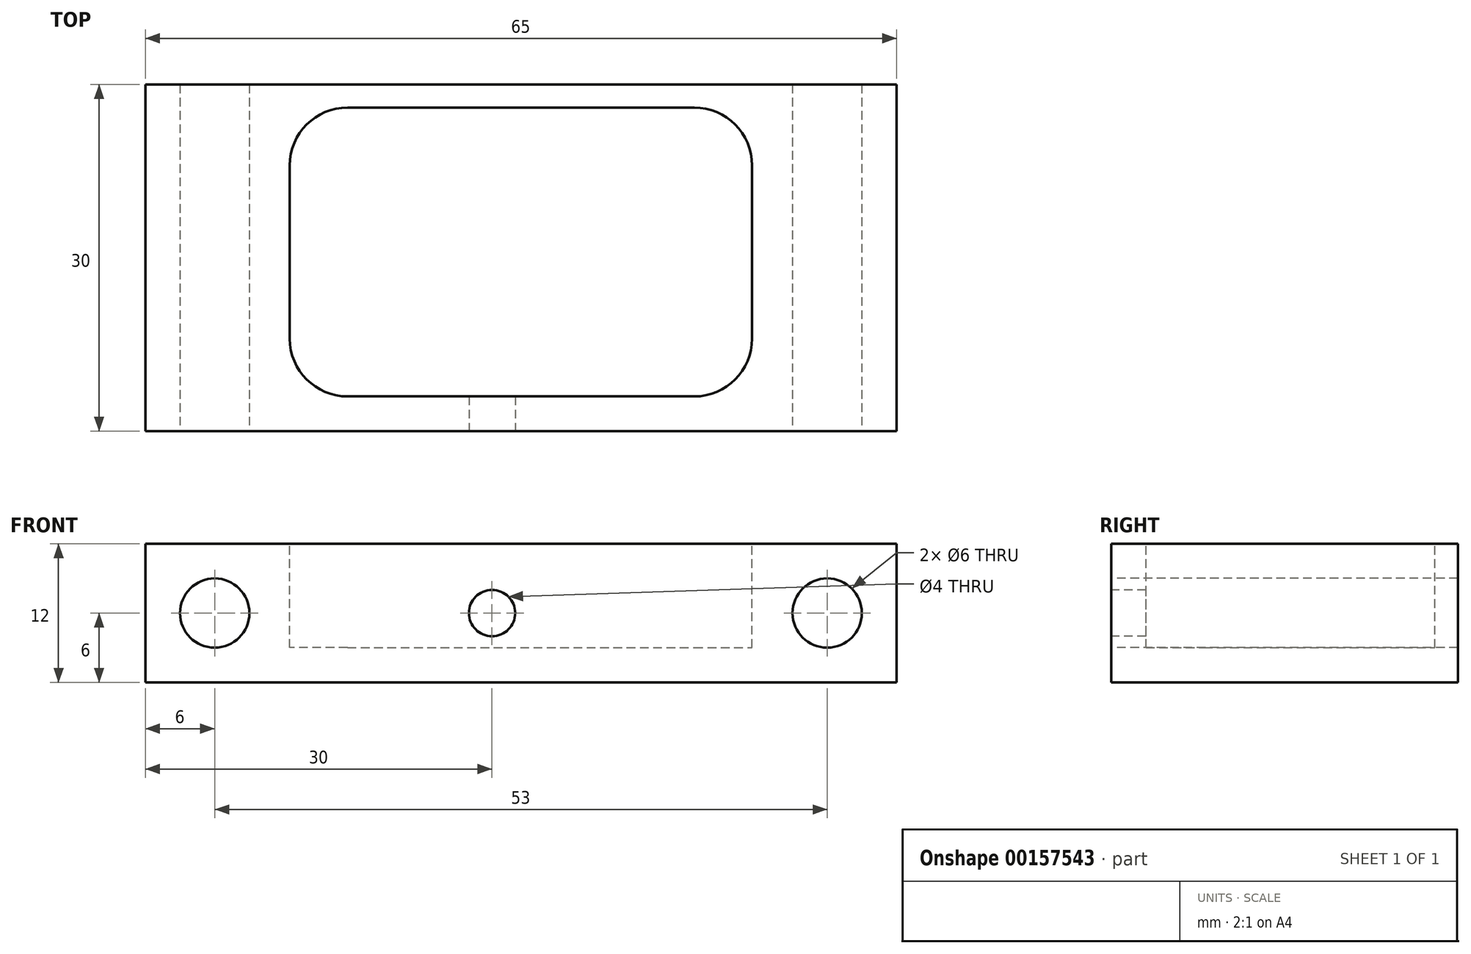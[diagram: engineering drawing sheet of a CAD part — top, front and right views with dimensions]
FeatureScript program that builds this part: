
annotation { "Feature Type Name" : "Feature", "Feature Type Description" : "" }
export const myFeature = defineFeature(function(context is Context, id is Id, definition is map)
    precondition{}
    {
        {
            var Q0;
            Q0=qCreatedBy(makeId("Top.planeOp"),FACE);
            var sketch = newSketch(context, id + "F0", { "sketchPlane" : qUnion([Q0])});
            skLineSegment(sketch, "E0.bottom", {"start": v(-22.35, 5.59) * mm, "end": v(42.65, 5.59) * mm});
            skLineSegment(sketch, "E0.top", {"start": v(-22.35, -24.41) * mm, "end": v(42.65, -24.41) * mm});
            skLineSegment(sketch, "E0.left", {"start": v(-22.35, 5.59) * mm, "end": v(-22.35, -24.41) * mm});
            skLineSegment(sketch, "E0.right", {"start": v(42.65, 5.59) * mm, "end": v(42.65, -24.41) * mm});
            skSolve(sketch);
        }
        {
            var Q0;
            {var subQ2=sQuery(id+"F0.wireOp",EDGE,"E0.bottom");Q0=makeQuery(id+"F0.imprint","IMPRINT",FACE,{"disambiguationData":[TD([[makeQuery(id+"F0.imprint","IMPRINT",EDGE,{"derivedFrom":subQ2}),-1.0]])]});}
            extrude(context, id + "F1", {"entities" : qUnion([Q0]), "depth" : 12 * mm});
        }
        {
            var Q0;
            Q0=makeQuery(id+"F1.opExtrude","SWEPT_FACE",FACE,{"disambiguationData":[OSD([sQuery(id+"F0.wireOp",EDGE,"E0.top")])]});
            cPlane(context, id + "F2", {"entities" : qUnion([Q0]), "cplaneType" : CPlaneType.OFFSET, "offset" : 0 * mm, "width" : 150 * mm, "height" : 150 * mm});
        }
        {
            var Q0;
            Q0=qCreatedBy(id+"F2.planeOp",FACE);
            var sketch = newSketch(context, id + "F3", { "sketchPlane" : qUnion([Q0])});
            skPoint(sketch, "E1", {"position": v(36.65, 6) * mm});
            skPoint(sketch, "E2", {"position": v(-16.35, 6) * mm});
            skPoint(sketch, "E3", {"position": v(7.65, 6) * mm});
            skPoint(sketch, "E4", {"position": v(22.65, 6) * mm});
            skSolve(sketch);
        }
        {
            var Q0;
            Q0=sQuery(id+"F3.wireOp",VERTEX,"E1");
            var Q1;
            Q1=makeQuery(id+"F1.opExtrude","SWEPT_BODY",BODY,{"disambiguationData":[OSD([sQuery(id+"F0.wireOp",EDGE,"E0.bottom"),sQuery(id+"F0.wireOp",EDGE,"E0.top"),sQuery(id+"F0.wireOp",EDGE,"E0.left"),sQuery(id+"F0.wireOp",EDGE,"E0.right"),sQuery(id+"F0.wireOp",EDGE,"GgG5EI5i-5B8A-6jPn-dVoJ-wmOckrl8psMe.bottom"),sQuery(id+"F0.wireOp",EDGE,"GgG5EI5i-5B8A-6jPn-dVoJ-wmOckrl8psMe.top"),sQuery(id+"F0.wireOp",EDGE,"GgG5EI5i-5B8A-6jPn-dVoJ-wmOckrl8psMe.right"),sQuery(id+"F0.wireOp",EDGE,"SIxaKF13-XDkE-nVYU-JOFU-2NFq09ALrB6F.bottom"),sQuery(id+"F0.wireOp",EDGE,"SIxaKF13-XDkE-nVYU-JOFU-2NFq09ALrB6F.top"),sQuery(id+"F0.wireOp",EDGE,"SIxaKF13-XDkE-nVYU-JOFU-2NFq09ALrB6F.left"),sQuery(id+"F0.wireOp",EDGE,"SIxaKF13-XDkE-nVYU-JOFU-2NFq09ALrB6F.right")])]});
            hole(context, id + "F4", {"style" : HoleStyle.SIMPLE, "endStyle" : HoleEndStyle.THROUGH, "holeDiameter" : 6 * mm, "startFromSketch" : true, "locations" : qUnion([Q0]), "scope" : qUnion([Q1]), "tappedDepth" : 12 * mm, "tapClearance" : 3});
        }
        {
            var Q0;
            Q0=sQuery(id+"F3.wireOp",VERTEX,"E2");
            var Q1;
            Q1=makeQuery(id+"F1.opExtrude","SWEPT_BODY",BODY,{"disambiguationData":[OSD([sQuery(id+"F0.wireOp",EDGE,"E0.bottom"),sQuery(id+"F0.wireOp",EDGE,"E0.top"),sQuery(id+"F0.wireOp",EDGE,"E0.left"),sQuery(id+"F0.wireOp",EDGE,"E0.right"),sQuery(id+"F0.wireOp",EDGE,"GgG5EI5i-5B8A-6jPn-dVoJ-wmOckrl8psMe.bottom"),sQuery(id+"F0.wireOp",EDGE,"GgG5EI5i-5B8A-6jPn-dVoJ-wmOckrl8psMe.top"),sQuery(id+"F0.wireOp",EDGE,"GgG5EI5i-5B8A-6jPn-dVoJ-wmOckrl8psMe.right"),sQuery(id+"F0.wireOp",EDGE,"SIxaKF13-XDkE-nVYU-JOFU-2NFq09ALrB6F.bottom"),sQuery(id+"F0.wireOp",EDGE,"SIxaKF13-XDkE-nVYU-JOFU-2NFq09ALrB6F.top"),sQuery(id+"F0.wireOp",EDGE,"SIxaKF13-XDkE-nVYU-JOFU-2NFq09ALrB6F.left"),sQuery(id+"F0.wireOp",EDGE,"SIxaKF13-XDkE-nVYU-JOFU-2NFq09ALrB6F.right")])]});
            hole(context, id + "F5", {"style" : HoleStyle.SIMPLE, "endStyle" : HoleEndStyle.THROUGH, "holeDiameter" : 6 * mm, "startFromSketch" : true, "locations" : qUnion([Q0]), "scope" : qUnion([Q1]), "isTappedThrough" : true});
        }
        {
            var Q0;
            Q0=makeQuery(id+"F1.opExtrude","CAP_FACE",FACE,{"disambiguationData":[OSD([sQuery(id+"F0.wireOp",EDGE,"E0.bottom"),sQuery(id+"F0.wireOp",EDGE,"E0.top"),sQuery(id+"F0.wireOp",EDGE,"E0.left"),sQuery(id+"F0.wireOp",EDGE,"E0.right")])],"isStart":false});
            var sketch = newSketch(context, id + "F6", { "sketchPlane" : qUnion([Q0])});
            skLineSegment(sketch, "E5.bottom", {"start": v(-9.85, -21.41) * mm, "end": v(30.15, -21.41) * mm});
            skLineSegment(sketch, "E5.top", {"start": v(-9.85, 3.59) * mm, "end": v(30.15, 3.59) * mm});
            skLineSegment(sketch, "E5.left", {"start": v(-9.85, -21.41) * mm, "end": v(-9.85, 3.59) * mm});
            skLineSegment(sketch, "E5.right", {"start": v(30.15, -21.41) * mm, "end": v(30.15, 3.59) * mm});
            skSolve(sketch);
        }
        {
            var Q0;
            Q0=makeQuery(id+"F6.imprint","IMPRINT",FACE,{"disambiguationData":[TD([[makeQuery(id+"F6.imprint","IMPRINT",EDGE,{"derivedFrom":sQuery(id+"F6.wireOp",EDGE,"E5.bottom")}),1.0]])]});
            extrude(context, id + "F7", {"entities" : qUnion([Q0]), "operationType" : NewBodyOperationType.REMOVE, "oppositeDirection" : true, "depth" : 9 * mm});
        }
        {
            var Q0;
            Q0=makeQuery(id+"F7.boolean.opBoolean","COPY",EDGE,{"derivedFrom":makeQuery(id+"F7.opExtrude","SWEPT_EDGE",EDGE,{"disambiguationData":[OSD([sQuery(id+"F6.wireOp",EDGE,"E5.top"),sQuery(id+"F6.wireOp",EDGE,"E5.left")])]})});
            var Q1;
            Q1=makeQuery(id+"F7.boolean.opBoolean","COPY",EDGE,{"derivedFrom":makeQuery(id+"F7.opExtrude","SWEPT_EDGE",EDGE,{"disambiguationData":[OSD([sQuery(id+"F6.wireOp",EDGE,"E5.bottom"),sQuery(id+"F6.wireOp",EDGE,"E5.left")])]})});
            var Q2;
            Q2=makeQuery(id+"F7.boolean.opBoolean","COPY",EDGE,{"derivedFrom":makeQuery(id+"F7.opExtrude","SWEPT_EDGE",EDGE,{"disambiguationData":[OSD([sQuery(id+"F6.wireOp",EDGE,"E5.top"),sQuery(id+"F6.wireOp",EDGE,"E5.right")])]})});
            var Q3;
            Q3=makeQuery(id+"F1.opExtrude","SWEPT_EDGE",EDGE,{"disambiguationData":[OSD([sQuery(id+"F0.wireOp",EDGE,"GgG5EI5i-5B8A-6jPn-dVoJ-wmOckrl8psMe.top"),sQuery(id+"F0.wireOp",EDGE,"GgG5EI5i-5B8A-6jPn-dVoJ-wmOckrl8psMe.right")])]});
            var Q4;
            Q4=makeQuery(id+"F1.opExtrude","SWEPT_EDGE",EDGE,{"disambiguationData":[OSD([sQuery(id+"F0.wireOp",EDGE,"GgG5EI5i-5B8A-6jPn-dVoJ-wmOckrl8psMe.bottom"),sQuery(id+"F0.wireOp",EDGE,"GgG5EI5i-5B8A-6jPn-dVoJ-wmOckrl8psMe.right")])]});
            var Q5;
            Q5=makeQuery(id+"F7.boolean.opBoolean","COPY",EDGE,{"derivedFrom":makeQuery(id+"F7.opExtrude","SWEPT_EDGE",EDGE,{"disambiguationData":[OSD([sQuery(id+"F6.wireOp",EDGE,"E5.bottom"),sQuery(id+"F6.wireOp",EDGE,"E5.right")])]})});
            fillet(context, id + "F8", {"entities" : qUnion([Q0, Q1, Q2, Q3, Q4, Q5]), "radius" : 5 * mm, "allowEdgeOverflow" : false});
        }
        {
            var Q0;
            Q0=sQuery(id+"F3.wireOp",VERTEX,"E3");
            var Q1;
            Q1=makeQuery(id+"F1.opExtrude","SWEPT_BODY",BODY,{"disambiguationData":[OSD([sQuery(id+"F0.wireOp",EDGE,"E0.bottom"),sQuery(id+"F0.wireOp",EDGE,"E0.top"),sQuery(id+"F0.wireOp",EDGE,"E0.left"),sQuery(id+"F0.wireOp",EDGE,"E0.right")])]});
            hole(context, id + "F9", {"style" : HoleStyle.SIMPLE, "endStyle" : HoleEndStyle.BLIND, "standardTappedOrClearance" : lookupTablePath({ "standard" : "ISO", "engagement" : "75%", "pitch" : "1 mm", "size" : "M5", "type" : "Tapped" }), "standardBlindInLast" : lookupTablePath({ "standard" : "ISO", "engagement" : "75%", "pitch" : "1 mm", "size" : "M5", "type" : "Tapped" }), "holeDiameter" : 4 * mm, "holeDepth" : 7 * mm, "startFromSketch" : true, "locations" : qUnion([Q0]), "scope" : qUnion([Q1])});
        }
    });
